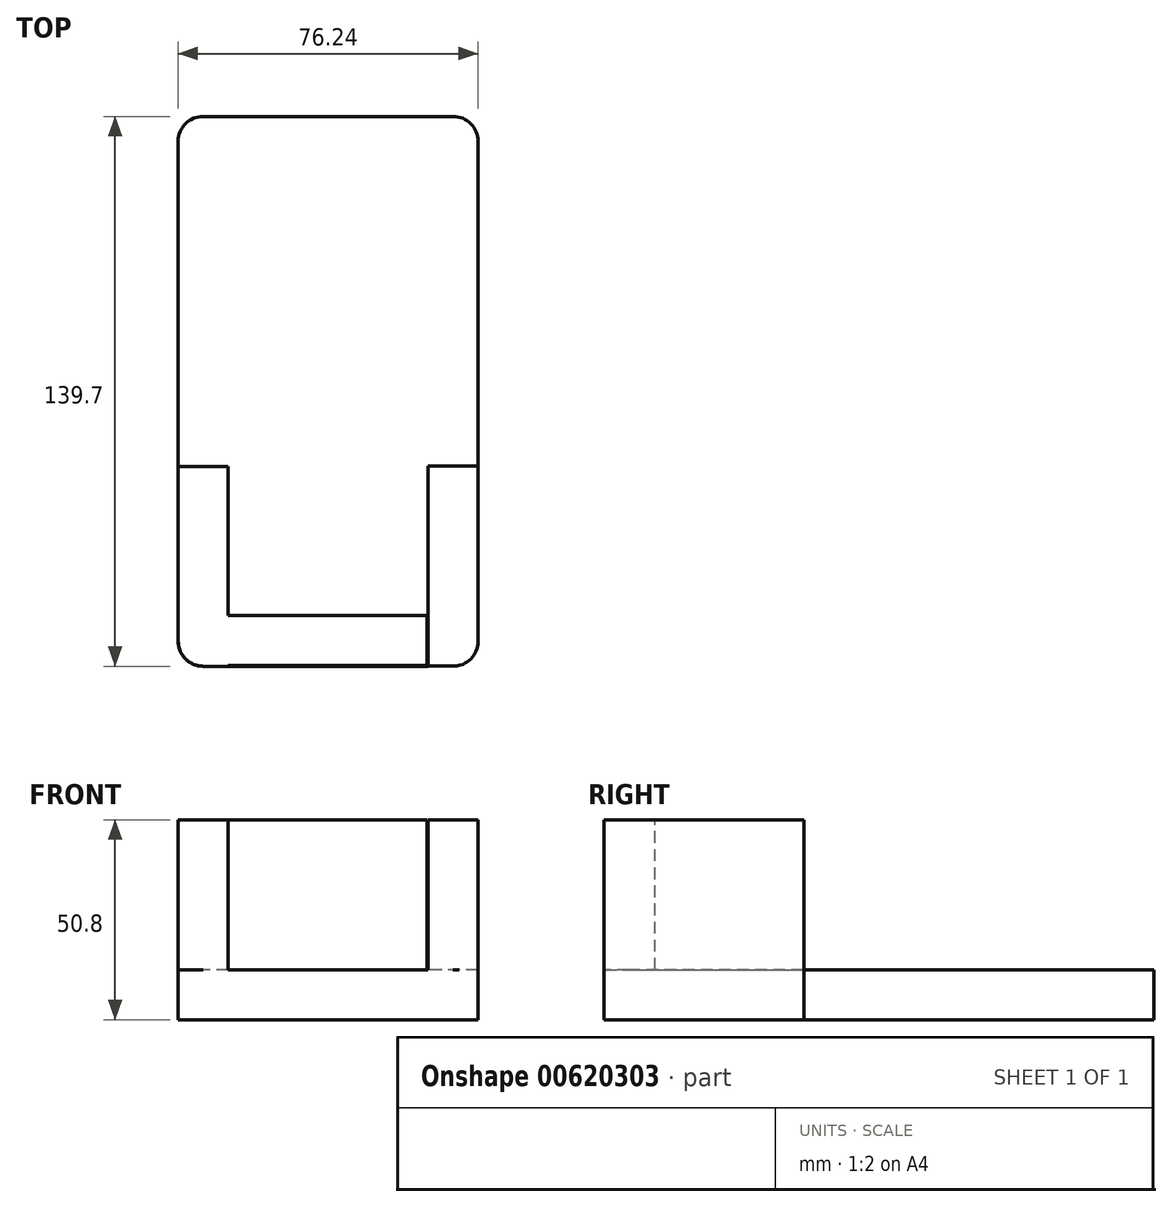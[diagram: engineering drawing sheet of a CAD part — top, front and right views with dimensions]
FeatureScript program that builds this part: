
annotation { "Feature Type Name" : "Feature", "Feature Type Description" : "" }
export const myFeature = defineFeature(function(context is Context, id is Id, definition is map)
    precondition{}
    {
        {
            var Q0;
            Q0=qCreatedBy(makeId("Top.planeOp"),FACE);
            var sketch = newSketch(context, id + "F0", { "sketchPlane" : qUnion([Q0])});
            skLineSegment(sketch, "E0.bottom", {"start": v(31.75, 69.85) * mm, "end": v(-31.75, 69.85) * mm});
            skLineSegment(sketch, "E0.top", {"start": v(31.75, -69.85) * mm, "end": v(-31.75, -69.85) * mm});
            skLineSegment(sketch, "E0.left", {"start": v(38.1, 63.5) * mm, "end": v(38.1, -63.5) * mm});
            skLineSegment(sketch, "E0.right", {"start": v(-38.1, 63.5) * mm, "end": v(-38.1, -63.5) * mm});
            skPoint(sketch, "E0.middle", {"position": v(0, 0) * mm});
            skPoint(sketch, "E1.visualSharp", {"position": v(38.1, 69.85) * mm});
            skArc(sketch, "E1.filletArc", {"start": v(38.1, 63.5) * mm, "mid": v(36.24, 68) * mm, "end": v(31.75, 69.85) * mm});
            skPoint(sketch, "E2.visualSharp", {"position": v(-38.1, 69.85) * mm});
            skArc(sketch, "E2.filletArc", {"start": v(-31.75, 69.85) * mm, "mid": v(-36.24, 68) * mm, "end": v(-38.1, 63.5) * mm});
            skPoint(sketch, "E3.visualSharp", {"position": v(38.1, -69.85) * mm});
            skArc(sketch, "E3.filletArc", {"start": v(31.75, -69.85) * mm, "mid": v(36.24, -68) * mm, "end": v(38.1, -63.5) * mm});
            skPoint(sketch, "E4.visualSharp", {"position": v(-38.1, -69.85) * mm});
            skArc(sketch, "E4.filletArc", {"start": v(-38.1, -63.5) * mm, "mid": v(-36.24, -68) * mm, "end": v(-31.75, -69.85) * mm});
            skSolve(sketch);
        }
        {
            var Q0;
            Q0=makeQuery(id+"F0.imprint","IMPRINT",FACE,{"disambiguationData":[TD([[makeQuery(id+"F0.imprint","IMPRINT",EDGE,{"derivedFrom":sQuery(id+"F0.wireOp",EDGE,"E0.bottom")}),1.0]])]});
            extrude(context, id + "F1", {"entities" : qUnion([Q0]), "depth" : 12.7 * mm, "offsetDistance" : 25.4 * mm});
        }
        {
            var Q0;
            Q0=qCreatedBy(makeId("Top.planeOp"),FACE);
            var sketch = newSketch(context, id + "F2", { "sketchPlane" : qUnion([Q0])});
            skLineSegment(sketch, "E5.bottom", {"start": v(-38.06, -19.05) * mm, "end": v(-25.36, -19.05) * mm});
            skLineSegment(sketch, "E5.top", {"start": v(-31.7, -69.85) * mm, "end": v(-25.36, -69.85) * mm});
            skLineSegment(sketch, "E5.left", {"start": v(-38.06, -19.05) * mm, "end": v(-38.06, -63.5) * mm});
            skLineSegment(sketch, "E5.right", {"start": v(-25.36, -19.05) * mm, "end": v(-25.36, -69.85) * mm});
            skLineSegment(sketch, "E6.bottom", {"start": v(25.44, -19.04) * mm, "end": v(38.14, -19.04) * mm});
            skLineSegment(sketch, "E6.top", {"start": v(25.44, -69.84) * mm, "end": v(31.8, -69.84) * mm});
            skLineSegment(sketch, "E6.left", {"start": v(25.44, -19.04) * mm, "end": v(25.44, -69.84) * mm});
            skLineSegment(sketch, "E6.right", {"start": v(38.14, -19.04) * mm, "end": v(38.14, -63.5) * mm});
            skPoint(sketch, "E7.visualSharp", {"position": v(-38.06, -69.85) * mm});
            skArc(sketch, "E7.filletArc", {"start": v(-38.06, -63.5) * mm, "mid": v(-36.2, -68) * mm, "end": v(-31.7, -69.85) * mm});
            skPoint(sketch, "E8.visualSharp", {"position": v(38.14, -69.84) * mm});
            skArc(sketch, "E8.filletArc", {"start": v(31.8, -69.84) * mm, "mid": v(36.28, -67.98) * mm, "end": v(38.14, -63.5) * mm});
            skSolve(sketch);
        }
        {
            var Q0;
            Q0=makeQuery(id+"F2.imprint","IMPRINT",FACE,{"disambiguationData":[TD([[makeQuery(id+"F2.imprint","IMPRINT",EDGE,{"derivedFrom":sQuery(id+"F2.wireOp",EDGE,"E5.bottom")}),-1.0]])]});
            var Q1;
            Q1=makeQuery(id+"F2.imprint","IMPRINT",FACE,{"disambiguationData":[TD([[makeQuery(id+"F2.imprint","IMPRINT",EDGE,{"derivedFrom":sQuery(id+"F2.wireOp",EDGE,"E6.bottom")}),-1.0]])]});
            extrude(context, id + "F3", {"entities" : qUnion([Q0, Q1]), "operationType" : NewBodyOperationType.ADD, "depth" : 50.8 * mm, "offsetDistance" : 25.4 * mm});
        }
        {
            var Q0;
            Q0=qCreatedBy(makeId("Top.planeOp"),FACE);
            var sketch = newSketch(context, id + "F4", { "sketchPlane" : qUnion([Q0])});
            skLineSegment(sketch, "E9.bottom", {"start": v(-25.67, -56.96) * mm, "end": v(25.13, -56.96) * mm});
            skLineSegment(sketch, "E9.top", {"start": v(-25.67, -69.66) * mm, "end": v(25.13, -69.66) * mm});
            skLineSegment(sketch, "E9.left", {"start": v(-25.67, -56.96) * mm, "end": v(-25.67, -69.66) * mm});
            skLineSegment(sketch, "E9.right", {"start": v(25.13, -56.96) * mm, "end": v(25.13, -69.66) * mm});
            skSolve(sketch);
        }
        {
            var Q0;
            Q0 = qSketchRegion(id + "F4", true);
            extrude(context, id + "F5", {"entities" : qUnion([Q0]), "operationType" : NewBodyOperationType.ADD, "depth" : 50.8 * mm, "offsetDistance" : 25.4 * mm});
        }
    });
